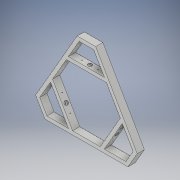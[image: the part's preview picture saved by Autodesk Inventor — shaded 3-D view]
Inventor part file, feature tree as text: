
AUTODESK INVENTOR PART (.ipt)
format: ipt  version: 2018 (Build 220112000, 112)  size: 249,344 bytes
history: native  units: in
note: dims shown in document units (in); Inventor stores cm internally (conversion verified against a paired STEP export)
features: extrude x6, sketch x6, shell x1
ambient origin geometry x8: Origin, YZ Plane, XZ Plane, XY Plane, X Axis, Y Axis, Z Axis, Center Point
bodies: Solid1 (feature_tree)
feature tree (13):
  extrude  "Extrusion1"  Depth=6.0in
  extrude  "Extrusion2"  Depth=6.0in
  extrude  "Extrusion3"  Depth=1.0in
  sketch  "Sketch4"  dims[d24=2.0in d25=0.0in d26=2.0in d27=0.0in]
  shell  "Shell1"  Thickness=1.1811in
  extrude  "Extrusion4"  Depth=2.0in TaperAngle=0.0deg
  extrude  "Extrusion5"  Depth=1.0in
  extrude  "Extrusion6"  Depth=1.0in
  sketch  "Sketch1"  dims[d0=10.0in d1=6.0in]
  sketch  "Sketch2"  dims[d2=60.0deg d3=6.0in]
  sketch  "Sketch3"  dims[d4=60.0deg d11=1.0in d20=1.1811in d22=360.0deg]
  sketch  "Sketch5"  dims[d28=2.0in d29=0.0in d30=1.0in]
  sketch  "Sketch6"  dims[d31=90.0deg d32=1.125in d33=0.0625in d34=2.25in d35=2.25in d36=0.196in d37=0.196in d38=1.0in d39=0.0in d40=1.0in d41=180.0deg d42=2.25in d43=2.25in d44=0.196in d45=0.196in d46=1.125in d47=1.0in d48=0.0in d49=1.0in d50=0.0in d51=2.25in d52=4.5in d53=0.196in d54=0.196in d55=1.125in d56=1.0in d57=0.0in]
